# Revit family: Verbundanker V, gvz
name_source: partatom
category: HLS-Bauteile
revit_build: Autodesk Revit 2017 (Build: 20190507_1515(x64)
units: mm (PartAtom-declared; Revit-internal decimal feet)

## family parameters
Basisbauteil = Fläche
Beim Laden mit Abzugskörper schneiden = Nein
Bemaßung runder Anschluss = Durchmesser verwenden
Gemeinsam genutzt = Ja
Raumberechnungspunkt = Nein
Teiletyp = Normal

## types (5) — shared parameters
Fabrikat = MKT
Firma = MEFA Befestigungs- und Montagesysteme GmbH
Material = Stahl
Mengeneinheit = St
Oberflaeche = galvanisch verzinkt
Vorgabe-Ansicht = 1219 mm
vpe = 10 St
zero-valued in all types: Länge Dübel

## per-type parameters (varying)
| type | Artikelnummer | Bohrerdurchmesser | Bohrlochtiefe | D | EAN | Gewicht | Gewicht pro Bauteil | Gewinde | Kurztext1 | Kurztext2 | L | L1 | L2 | Länge | Mutter | Unterlegscheibe | Verankerungstiefe |
| Ankerstange V-A  8- 20/110, gvz | 221821101101 | 10 mm | 80 mm | 7 mm  [stored 0.0229659 ft] | 4043315019288 | 0.04 kg | 0.04 kg | M8 | Ankerstange V A M8 | Länge 110 mm Stahl | 110 mm  [stored 0.360892 ft] | 95 mm | 15 mm  [stored 0.0492126 ft] | 110 mm  [stored 0.360892 ft] | Sechskantmutter : Sechskantmutter M8 | Unterlegscheibe : Unterlegscheibe 8.4x16x1.6 | 80 mm |
| Ankerstange V-A 10- 30/130, gvz | 221821203101 | 12 mm | 90 mm | 8 mm  [stored 0.0262467 ft] | 4043315019776 | 0.08 kg | 0.08 kg | M10 | Ankerstange V A M10 | Länge 130 mm Stahl | 130 mm  [stored 0.426509 ft] | 115 mm  [stored 0.377297 ft] | 15 mm  [stored 0.0492126 ft] | 130 mm  [stored 0.426509 ft] | Sechskantmutter : Sechskantmutter M10 | Unterlegscheibe : Unterlegscheibe 10.5x20x2 | 90 mm |
| Ankerstange V-A 10- 65/165, gvz | 221821207101 | 12 mm | 90 mm | 8 mm  [stored 0.0262467 ft] | 4043315019974 | 0.10 kg | 0.10 kg | M10 | Ankerstange V A M10 | Länge 165 mm Stahl | 165 mm  [stored 0.541339 ft] | 150 mm | 15 mm  [stored 0.0492126 ft] | 165 mm  [stored 0.541339 ft] | Sechskantmutter : Sechskantmutter M10 | Unterlegscheibe : Unterlegscheibe 10.5x20x2 | 90 mm |
| Ankerstange V-A 12- 35/160, gvz | 221821306101 | 14 mm | 110 mm | 10 mm  [stored 0.0328084 ft] | 4043315020512 | 0.14 kg | 0.14 kg | M12 | Ankerstange V A M12 | Länge 160 mm Stahl | 160 mm  [stored 0.524934 ft] | 145 mm  [stored 0.475722 ft] | 15 mm  [stored 0.0492126 ft] | 160 mm  [stored 0.524934 ft] | Sechskantmutter : Sechskantmutter M12 | Unterlegscheibe : Unterlegscheibe 13x24x2.5 | 110 mm |
| Ankerstange V-A 16- 20/165, gvz | 221821507101 | 18 mm | 125 mm | 14 mm  [stored 0.0459318 ft] | 4043315021564 | 0.28 kg | 0.28 kg | M16 | Ankerstange V A | Länge 165 mm Stahl | 165 mm  [stored 0.541339 ft] | 145 mm  [stored 0.475722 ft] | 20 mm  [stored 0.0656168 ft] | 165 mm  [stored 0.541339 ft] | Sechskantmutter : Sechskantmutter M16 | Unterlegscheibe : Unterlegscheibe, verstärkt 17x44x3.5 | 125 mm |

note: [stored X ft] marks values corroborated as IEEE doubles in the binary element streams (Revit-internal decimal feet)

## geometry (parser evidence)
native form markers: Sweep x2
no freeform markers — native parametric forms only
